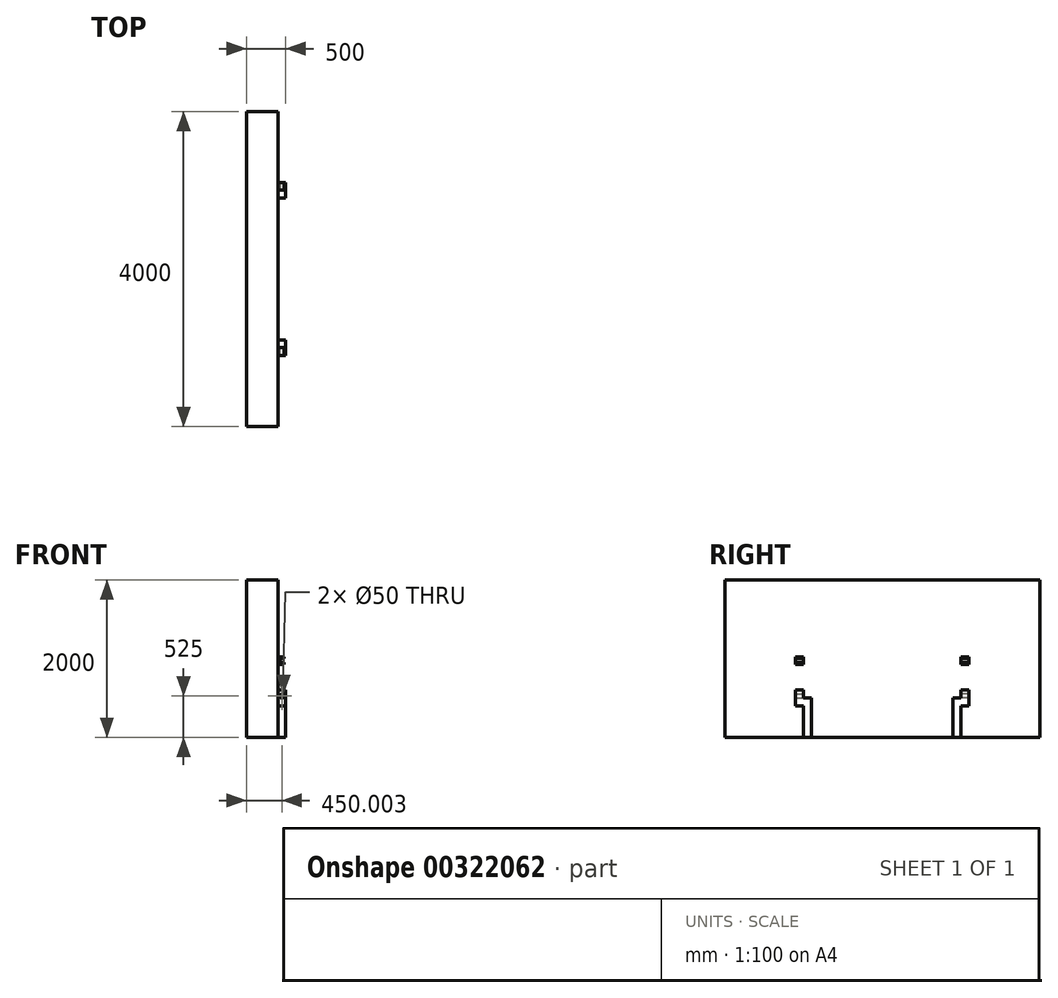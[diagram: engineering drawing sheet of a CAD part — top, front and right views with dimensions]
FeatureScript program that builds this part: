
annotation { "Feature Type Name" : "Feature", "Feature Type Description" : "" }
export const myFeature = defineFeature(function(context is Context, id is Id, definition is map)
    precondition{}
    {
        {
            var Q0;
            Q0=qCreatedBy(makeId("Top.planeOp"),FACE);
            var sketch = newSketch(context, id + "F0", { "sketchPlane" : qUnion([Q0])});
            skLineSegment(sketch, "E0.bottom", {"start": v(74.57, -1998.05) * mm, "end": v(-325.43, -1998.05) * mm});
            skLineSegment(sketch, "E0.top", {"start": v(74.57, 2001.95) * mm, "end": v(-325.43, 2001.95) * mm});
            skLineSegment(sketch, "E0.left", {"start": v(74.57, -1998.05) * mm, "end": v(74.57, 2001.95) * mm});
            skLineSegment(sketch, "E0.right", {"start": v(-325.43, -1998.05) * mm, "end": v(-325.43, 2001.95) * mm});
            skPoint(sketch, "E0.middle", {"position": v(-125.43, 1.95) * mm});
            skLineSegment(sketch, "E1.bottom", {"start": v(74.57, -998.05) * mm, "end": v(174.57, -998.05) * mm});
            skLineSegment(sketch, "E1.top", {"start": v(74.57, -898.05) * mm, "end": v(174.57, -898.05) * mm});
            skLineSegment(sketch, "E1.left", {"start": v(74.57, -998.05) * mm, "end": v(74.57, -898.05) * mm});
            skLineSegment(sketch, "E1.right", {"start": v(174.57, -998.05) * mm, "end": v(174.57, -898.05) * mm});
            skLineSegment(sketch, "E2.bottom", {"start": v(74.57, 1001.95) * mm, "end": v(174.57, 1001.95) * mm});
            skLineSegment(sketch, "E2.top", {"start": v(74.57, 901.95) * mm, "end": v(174.57, 901.95) * mm});
            skLineSegment(sketch, "E2.left", {"start": v(74.57, 1001.95) * mm, "end": v(74.57, 901.95) * mm});
            skLineSegment(sketch, "E2.right", {"start": v(174.57, 1001.95) * mm, "end": v(174.57, 901.95) * mm});
            skSolve(sketch);
        }
        {
            var Q0;
            {var subQ3=sQuery(id+"F0.wireOp",EDGE,"E0.bottom");Q0=makeQuery(id+"F0.imprint","IMPRINT",FACE,{"disambiguationData":[TD([[makeQuery(id+"F0.imprint","IMPRINT",EDGE,{"derivedFrom":subQ3}),-1.0]])]});}
            extrude(context, id + "F1", {"entities" : qUnion([Q0]), "depth" : 2000 * mm});
        }
        {
            var Q0;
            Q0=makeQuery(id+"F0.imprint","IMPRINT",FACE,{"disambiguationData":[TD([[makeQuery(id+"F0.imprint","IMPRINT",EDGE,{"derivedFrom":sQuery(id+"F0.wireOp",EDGE,"E1.bottom")}),1.0]])]});
            var Q1;
            Q1=makeQuery(id+"F0.imprint","IMPRINT",FACE,{"disambiguationData":[TD([[makeQuery(id+"F0.imprint","IMPRINT",EDGE,{"derivedFrom":sQuery(id+"F0.wireOp",EDGE,"E2.bottom")}),-1.0]])]});
            extrude(context, id + "F2", {"entities" : qUnion([Q0, Q1]), "operationType" : NewBodyOperationType.ADD, "depth" : 500 * mm});
        }
        {
            var Q0;
            Q0=makeQuery(id+"F2.opExtrude","SWEPT_FACE",FACE,{"disambiguationData":[OSD([sQuery(id+"F0.wireOp",EDGE,"E1.bottom")])]});
            var sketch = newSketch(context, id + "F3", { "sketchPlane" : qUnion([Q0])});
            skLineSegment(sketch, "E3.bottom", {"start": v(74.57, 400) * mm, "end": v(174.57, 400) * mm});
            skLineSegment(sketch, "E3.top", {"start": v(74.57, 600) * mm, "end": v(174.57, 600) * mm});
            skLineSegment(sketch, "E3.left", {"start": v(74.57, 400) * mm, "end": v(74.57, 600) * mm});
            skLineSegment(sketch, "E3.right", {"start": v(174.57, 400) * mm, "end": v(174.57, 600) * mm});
            skCircle(sketch, "E4", {"center": v(124.57, 525) * mm, "radius": 25 * mm});
            skPoint(sketch, "E4.centerSnap0", {"position": v(124.57, 600) * mm});
            skSolve(sketch);
        }
        {
            var Q0;
            Q0=makeQuery(id+"F2.opExtrude","SWEPT_FACE",FACE,{"disambiguationData":[OSD([sQuery(id+"F0.wireOp",EDGE,"E2.bottom")])]});
            var sketch = newSketch(context, id + "F4", { "sketchPlane" : qUnion([Q0])});
            skLineSegment(sketch, "E5.bottom", {"start": v(-74.57, 400) * mm, "end": v(-174.57, 400) * mm});
            skLineSegment(sketch, "E5.top", {"start": v(-74.57, 600) * mm, "end": v(-174.57, 600) * mm});
            skLineSegment(sketch, "E5.left", {"start": v(-74.57, 400) * mm, "end": v(-74.57, 600) * mm});
            skLineSegment(sketch, "E5.right", {"start": v(-174.57, 400) * mm, "end": v(-174.57, 600) * mm});
            skCircle(sketch, "E6", {"center": v(-124.57, 525) * mm, "radius": 25 * mm});
            skPoint(sketch, "E6.centerSnap0", {"position": v(-124.57, 600) * mm});
            skSolve(sketch);
        }
        {
            var Q0;
            {var subQ0=sQuery(id+"F4.wireOp",EDGE,"E5.bottom");Q0=makeQuery(id+"F4.imprint","IMPRINT",FACE,{"disambiguationData":[TD([[makeQuery(id+"F4.imprint","IMPRINT",EDGE,{"derivedFrom":subQ0}),-1.0]])]});}
            var Q1;
            {var subQ0=sQuery(id+"F4.wireOp",EDGE,"E5.top");Q1=makeQuery(id+"F4.imprint","IMPRINT",FACE,{"disambiguationData":[TD([[makeQuery(id+"F4.imprint","IMPRINT",EDGE,{"derivedFrom":subQ0}),1.0]])]});}
            extrude(context, id + "F5", {"entities" : qUnion([Q0, Q1]), "operationType" : NewBodyOperationType.ADD, "depth" : 100 * mm});
        }
        {
            var Q0;
            {var subQ0=sQuery(id+"F3.wireOp",EDGE,"E3.top");Q0=makeQuery(id+"F3.imprint","IMPRINT",FACE,{"disambiguationData":[TD([[makeQuery(id+"F3.imprint","IMPRINT",EDGE,{"derivedFrom":subQ0}),-1.0]])]});}
            var Q1;
            {var subQ0=sQuery(id+"F3.wireOp",EDGE,"E3.bottom");Q1=makeQuery(id+"F3.imprint","IMPRINT",FACE,{"disambiguationData":[TD([[makeQuery(id+"F3.imprint","IMPRINT",EDGE,{"derivedFrom":subQ0}),1.0]])]});}
            extrude(context, id + "F6", {"entities" : qUnion([Q0, Q1]), "operationType" : NewBodyOperationType.ADD, "depth" : 100 * mm});
        }
        {
            var Q0;
            Q0=makeQuery(id+"F1.opExtrude","SWEPT_FACE",FACE,{"disambiguationData":[OSD([sQuery(id+"F0.wireOp",EDGE,"E0.left"),sQuery(id+"F0.wireOp",EDGE,"E1.left"),sQuery(id+"F0.wireOp",EDGE,"E2.left")])]});
            var sketch = newSketch(context, id + "F7", { "sketchPlane" : qUnion([Q0])});
            skLineSegment(sketch, "E7.bottom", {"start": v(-1098.05, 1025) * mm, "end": v(-998.05, 1025) * mm});
            skLineSegment(sketch, "E7.top", {"start": v(-1098.05, 925) * mm, "end": v(-998.05, 925) * mm});
            skLineSegment(sketch, "E7.left", {"start": v(-1098.05, 1025) * mm, "end": v(-1098.05, 925) * mm});
            skLineSegment(sketch, "E7.right", {"start": v(-998.05, 1025) * mm, "end": v(-998.05, 925) * mm});
            skLineSegment(sketch, "E8.bottom", {"start": v(1001.95, 1025) * mm, "end": v(1101.95, 1025) * mm});
            skLineSegment(sketch, "E8.top", {"start": v(1001.95, 925) * mm, "end": v(1101.95, 925) * mm});
            skLineSegment(sketch, "E8.left", {"start": v(1001.95, 1025) * mm, "end": v(1001.95, 925) * mm});
            skLineSegment(sketch, "E8.right", {"start": v(1101.95, 1025) * mm, "end": v(1101.95, 925) * mm});
            skSolve(sketch);
        }
        {
            var Q0;
            Q0 = qSketchRegion(id + "F7", true);
            extrude(context, id + "F8", {"entities" : qUnion([Q0]), "operationType" : NewBodyOperationType.ADD, "depth" : 75 * mm});
        }
        {
            var Q0;
            Q0=makeQuery(id+"F8.opExtrude","SWEPT_FACE",FACE,{"disambiguationData":[OSD([sQuery(id+"F7.wireOp",EDGE,"E8.right")])]});
            var sketch = newSketch(context, id + "F9", { "sketchPlane" : qUnion([Q0])});
            skCircle(sketch, "E9", {"center": v(-124.57, 975.95) * mm, "radius": 25 * mm});
            skLineSegment(sketch, "E10.bottom", {"start": v(-124.57, 1000.95) * mm, "end": v(-149.57, 1000.95) * mm});
            skLineSegment(sketch, "E10.right", {"start": v(-149.57, 1000.95) * mm, "end": v(-149.57, 950.95) * mm});
            skLineSegment(sketch, "E11", {"start": v(-149.57, 950.95) * mm, "end": v(-124.57, 950.95) * mm});
            skSolve(sketch);
        }
        {
            var Q0;
            Q0 = qSketchRegion(id + "F9", true);
            extrude(context, id + "F10", {"entities" : qUnion([Q0]), "operationType" : NewBodyOperationType.REMOVE, "oppositeDirection" : true, "depth" : 2277 * mm});
        }
    });
